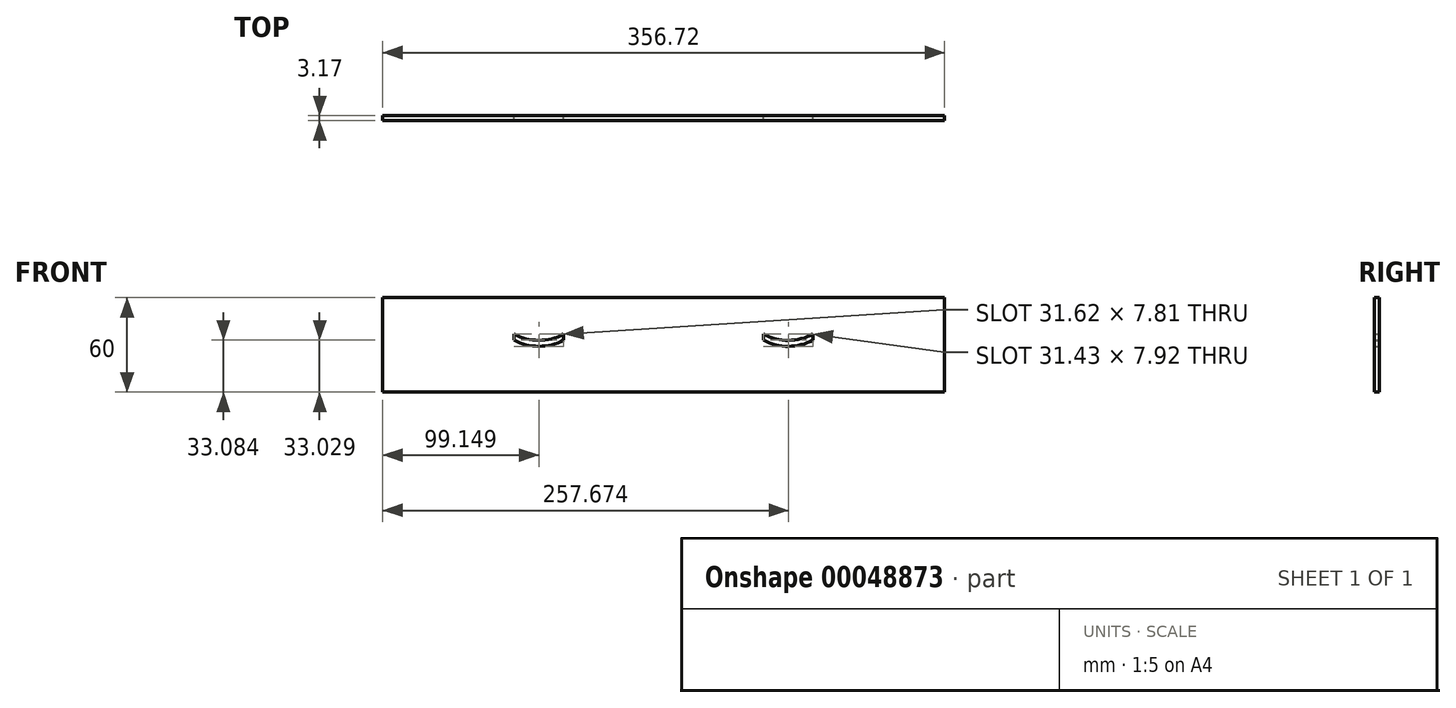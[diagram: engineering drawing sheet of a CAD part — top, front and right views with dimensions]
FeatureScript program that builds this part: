
annotation { "Feature Type Name" : "Feature", "Feature Type Description" : "" }
export const myFeature = defineFeature(function(context is Context, id is Id, definition is map)
    precondition{}
    {
        {
            var Q0;
            Q0=qCreatedBy(makeId("Front.planeOp"),FACE);
            var sketch = newSketch(context, id + "F0", { "sketchPlane" : qUnion([Q0])});
            skLineSegment(sketch, "E0.bottom", {"start": v(-51.61, 16.74) * mm, "end": v(98.39, 16.74) * mm});
            skLineSegment(sketch, "E0.top", {"start": v(-51.61, -43.26) * mm, "end": v(98.39, -43.26) * mm});
            skArc(sketch, "E1", {"start": v(-16.56, -6.32) * mm, "mid": v(-0.75, -10.33) * mm, "end": v(15.06, -6.32) * mm});
            skLineSegment(sketch, "E2", {"start": v(-16.56, -6.32) * mm, "end": v(-16.56, -10.13) * mm});
            skLineSegment(sketch, "E3", {"start": v(15.06, -6.32) * mm, "end": v(15.06, -10.13) * mm});
            skArc(sketch, "E4", {"start": v(-16.56, -10.13) * mm, "mid": v(-0.75, -14.14) * mm, "end": v(15.06, -10.13) * mm});
            skLineSegment(sketch, "E5.bottom", {"start": v(-51.61, -43.26) * mm, "end": v(-99.9, -43.26) * mm});
            skLineSegment(sketch, "E5.top", {"start": v(-51.61, 16.74) * mm, "end": v(-99.9, 16.74) * mm});
            skLineSegment(sketch, "E5.right", {"start": v(-99.9, -43.26) * mm, "end": v(-99.9, 16.74) * mm});
            skLineSegment(sketch, "E6", {"start": v(-0.75, -10.33) * mm, "end": v(-0.75, -14.14) * mm});
            skLineSegment(sketch, "E7", {"start": v(142.06, -6.32) * mm, "end": v(142.06, -10.13) * mm});
            skLineSegment(sketch, "E8", {"start": v(173.49, -6.21) * mm, "end": v(173.49, -10.02) * mm});
            skArc(sketch, "E9", {"start": v(142.06, -6.32) * mm, "mid": v(157.79, -10.33) * mm, "end": v(173.49, -6.21) * mm});
            skArc(sketch, "E10", {"start": v(142.06, -10.13) * mm, "mid": v(157.79, -14.14) * mm, "end": v(173.49, -10.02) * mm});
            skLineSegment(sketch, "E11", {"start": v(98.39, 16.74) * mm, "end": v(256.82, 16.74) * mm});
            skLineSegment(sketch, "E12", {"start": v(256.82, 16.74) * mm, "end": v(256.82, -43.26) * mm});
            skLineSegment(sketch, "E13", {"start": v(256.82, -43.26) * mm, "end": v(98.39, -43.26) * mm});
            skSolve(sketch);
        }
        {
            var Q0;
            Q0=makeQuery(id+"F0.imprint","IMPRINT",FACE,{"disambiguationData":[TD([[makeQuery(id+"F0.imprint","IMPRINT",EDGE,{"derivedFrom":sQuery(id+"F0.wireOp",EDGE,"E0.bottom")}),-1.0]])]});
            extrude(context, id + "F1", {"entities" : qUnion([Q0]), "depth" : 3.17 * mm});
        }
    });
